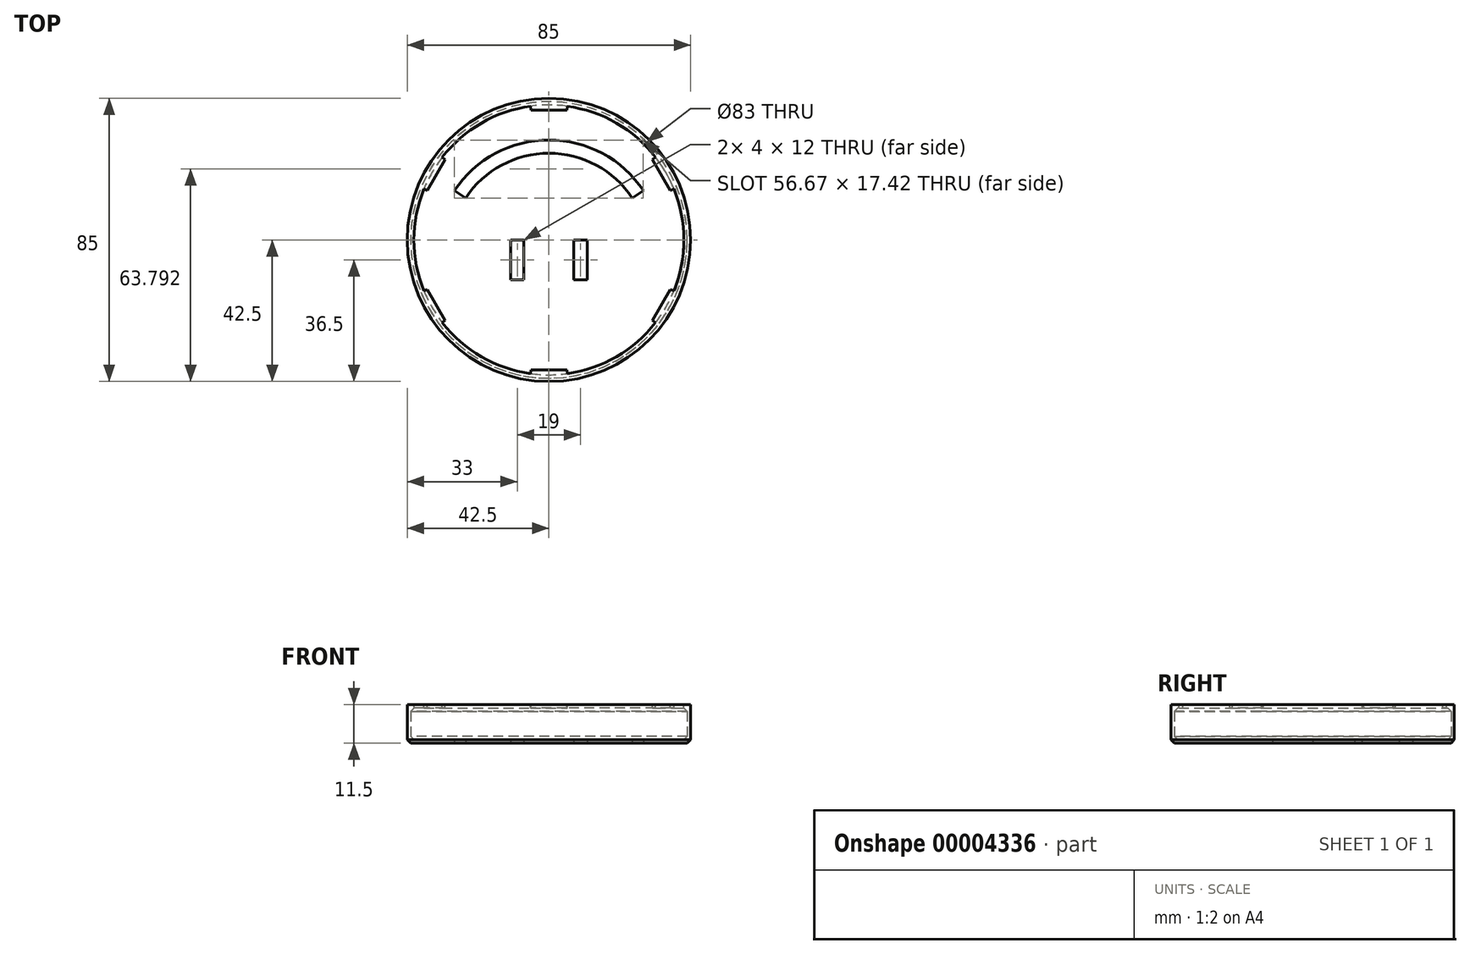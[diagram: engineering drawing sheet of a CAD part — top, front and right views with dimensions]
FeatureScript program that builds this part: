
annotation { "Feature Type Name" : "Feature", "Feature Type Description" : "" }
export const myFeature = defineFeature(function(context is Context, id is Id, definition is map)
    precondition{}
    {
        {
            var Q0;
            Q0=qCreatedBy(makeId("Top.planeOp"),FACE);
            var sketch = newSketch(context, id + "F0", { "sketchPlane" : qUnion([Q0])});
            skCircle(sketch, "E0", {"center": v(0, 0) * mm, "radius": 42.5 * mm});
            skSolve(sketch);
        }
        {
            var Q0;
            Q0 = qSketchRegion(id + "F0", true);
            extrude(context, id + "F1", {"entities" : qUnion([Q0]), "depth" : 11.5 * mm});
        }
        {
            var Q0;
            Q0=makeQuery(id+"F1.opExtrude","CAP_FACE",FACE,{"disambiguationData":[OSD([sQuery(id+"F0.wireOp",EDGE,"E0")])],"isStart":false});
            shell(context, id + "F2", {"entities" : qUnion([Q0]), "thickness" : 1 * mm});
        }
        {
            var Q0;
            Q0=makeQuery(id+"F1.opExtrude","CAP_FACE",FACE,{"disambiguationData":[OSD([sQuery(id+"F0.wireOp",EDGE,"E0")])],"isStart":false});
            var sketch = newSketch(context, id + "F3", { "sketchPlane" : qUnion([Q0])});
            skCircle(sketch, "E1", {"center": v(0, 0) * mm, "radius": 42.5 * mm});
            skCircle(sketch, "E2", {"center": v(0, 0) * mm, "radius": 40.5 * mm});
            skSolve(sketch);
        }
        {
            var Q0;
            Q0 = qSketchRegion(id + "F3", true);
            extrude(context, id + "F4", {"entities" : qUnion([Q0]), "operationType" : NewBodyOperationType.ADD, "oppositeDirection" : true, "depth" : 1 * mm});
        }
        {
            var Q0;
            Q0=makeQuery(id+"F4.boolean.opBoolean","MERGE",FACE,{"derivedFrom":[makeQuery(id+"F1.opExtrude","CAP_FACE",FACE,{"disambiguationData":[OSD([sQuery(id+"F0.wireOp",EDGE,"E0")])],"isStart":false}),makeQuery(id+"F4.opExtrude","CAP_FACE",FACE,{"disambiguationData":[OSD([sQuery(id+"F3.wireOp",EDGE,"E1"),sQuery(id+"F3.wireOp",EDGE,"E2")])],"isStart":true})]});
            var sketch = newSketch(context, id + "F5", { "sketchPlane" : qUnion([Q0])});
            skLineSegment(sketch, "E3", {"start": v(-5.5, 40.12) * mm, "end": v(-5.35, 39) * mm});
            skLineSegment(sketch, "E4", {"start": v(5.35, 39) * mm, "end": v(5.5, 40.12) * mm});
            skLineSegment(sketch, "E5", {"start": v(-5.5, 40.12) * mm, "end": v(-5.5, 40.5) * mm});
            skLineSegment(sketch, "E6", {"start": v(-5.5, 40.5) * mm, "end": v(5.5, 40.5) * mm});
            skLineSegment(sketch, "E7", {"start": v(5.5, 40.5) * mm, "end": v(5.5, 40.12) * mm});
            skLineSegment(sketch, "E8", {"start": v(-5.35, 39) * mm, "end": v(0, 39) * mm});
            skLineSegment(sketch, "E9", {"start": v(0, 39) * mm, "end": v(5.35, 39) * mm});
            skLineSegment(sketch, "E10", {"start": v(-5.5, 40.12) * mm, "end": v(-13.28, 39.06) * mm, "construction": true});
            skLineSegment(sketch, "E11", {"start": v(5.5, 40.12) * mm, "end": v(13.86, 38.98) * mm, "construction": true});
            skSolve(sketch);
        }
        {
            var Q0;
            Q0 = qSketchRegion(id + "F5", true);
            extrude(context, id + "F6", {"entities" : qUnion([Q0]), "operationType" : NewBodyOperationType.ADD, "oppositeDirection" : true, "depth" : 1 * mm});
        }
        {
            var Q0;
            Q0=qCreatedBy(makeId("Right.planeOp"),FACE);
            var sketch = newSketch(context, id + "F7", { "sketchPlane" : qUnion([Q0])});
            skLineSegment(sketch, "E12", {"start": v(0, 0) * mm, "end": v(0, 49.63) * mm, "construction": true});
            skSolve(sketch);
        }
        {
            var Q0;
            Q0=makeQuery(id+"F6.opExtrude","SWEPT_FACE",FACE,{"disambiguationData":[OSD([sQuery(id+"F5.wireOp",EDGE,"E4")])]});
            var Q1;
            Q1=makeQuery(id+"F6.opExtrude","SWEPT_FACE",FACE,{"disambiguationData":[OSD([sQuery(id+"F5.wireOp",EDGE,"E8"),sQuery(id+"F5.wireOp",EDGE,"E9")])]});
            var Q2;
            Q2=makeQuery(id+"F6.opExtrude","SWEPT_FACE",FACE,{"disambiguationData":[OSD([sQuery(id+"F5.wireOp",EDGE,"E3")])]});
            var Q3;
            Q3=sQuery(id+"F7.wireOp",EDGE,"E12");
            circularPattern(context, id + "F8", {"faces" : qUnion([Q0, Q1, Q2]), "axis" : qUnion([Q3]), "angle" : 60 * degree, "instanceCount" : 6, "patternType" : PatternType.FACE});
        }
        {
            var Q0;
            {var subQ0=sQuery(id+"F0.wireOp",EDGE,"E0");Q0=makeQuery(id+"F2.opShell","OFFSET_EDGE",EDGE,{"disambiguationData":[OSD([subQ0]),TDD([makeQuery(id+"F1.opExtrude","CAP_EDGE",EDGE,{"disambiguationData":[OSD([subQ0])],"isStart":true})])]});}
            chamfer(context, id + "F9", {"entities" : qUnion([Q0]), "width" : 1 * mm, "tangentPropagation" : true});
        }
        {
            var Q0;
            Q0=makeQuery(id+"F1.opExtrude","CAP_EDGE",EDGE,{"disambiguationData":[OSD([sQuery(id+"F0.wireOp",EDGE,"E0")])],"isStart":true});
            chamfer(context, id + "F10", {"entities" : qUnion([Q0]), "width" : 1 * mm, "tangentPropagation" : true});
        }
        {
            var Q0;
            Q0=makeQuery(id+"F1.opExtrude","CAP_FACE",FACE,{"disambiguationData":[OSD([sQuery(id+"F0.wireOp",EDGE,"E0")])],"isStart":true});
            var sketch = newSketch(context, id + "F11", { "sketchPlane" : qUnion([Q0])});
            skArc(sketch, "E13", {"start": v(-25, -12.58) * mm, "mid": v(0, -26) * mm, "end": v(25, -12.58) * mm});
            skArc(sketch, "E14", {"start": v(-28.33, -14.8) * mm, "mid": v(0, -30) * mm, "end": v(28.33, -14.8) * mm});
            skLineSegment(sketch, "E15", {"start": v(-28.33, -14.8) * mm, "end": v(-25, -12.58) * mm});
            skLineSegment(sketch, "E16", {"start": v(25, -12.58) * mm, "end": v(28.33, -14.8) * mm});
            skLineSegment(sketch, "E17", {"start": v(-28.33, -14.8) * mm, "end": v(0, -57.5) * mm, "construction": true});
            skLineSegment(sketch, "E18", {"start": v(0, -57.5) * mm, "end": v(28.33, -14.8) * mm, "construction": true});
            skLineSegment(sketch, "E19.bottom", {"start": v(-11.5, 12) * mm, "end": v(-7.5, 12) * mm});
            skLineSegment(sketch, "E19.top", {"start": v(-11.5, 0) * mm, "end": v(-7.5, 0) * mm});
            skLineSegment(sketch, "E19.left", {"start": v(-11.5, 12) * mm, "end": v(-11.5, 0) * mm});
            skLineSegment(sketch, "E19.right", {"start": v(-7.5, 12) * mm, "end": v(-7.5, 0) * mm});
            skLineSegment(sketch, "E20.bottom", {"start": v(7.5, 12) * mm, "end": v(11.5, 12) * mm});
            skLineSegment(sketch, "E20.top", {"start": v(7.5, 0) * mm, "end": v(11.5, 0) * mm});
            skLineSegment(sketch, "E20.left", {"start": v(7.5, 12) * mm, "end": v(7.5, 0) * mm});
            skLineSegment(sketch, "E20.right", {"start": v(11.5, 12) * mm, "end": v(11.5, 0) * mm});
            skLineSegment(sketch, "E21", {"start": v(0, 0) * mm, "end": v(0, 0) * mm});
            skLineSegment(sketch, "E22", {"start": v(0, 0) * mm, "end": v(7.5, 0) * mm, "construction": true});
            skLineSegment(sketch, "E23", {"start": v(0, 0) * mm, "end": v(-7.5, 0) * mm, "construction": true});
            skSolve(sketch);
        }
        {
            var Q0;
            Q0 = qSketchRegion(id + "F11", true);
            extrude(context, id + "F12", {"entities" : qUnion([Q0]), "operationType" : NewBodyOperationType.REMOVE, "oppositeDirection" : true, "depth" : 2 * mm});
        }
        {
            var Q0;
            {var subQ0=sQuery(id+"F0.wireOp",EDGE,"E0");Q0=makeQuery(id+"F4.boolean.opBoolean","INTERSECT",EDGE,{"derivedFrom":[makeQuery(id+"F2.opShell","OFFSET_FACE",FACE,{"disambiguationData":[OSD([subQ0]),TDD([makeQuery(id+"F1.opExtrude","SWEPT_FACE",FACE,{"disambiguationData":[OSD([subQ0])]})])]}),makeQuery(id+"F4.opExtrude","CAP_FACE",FACE,{"disambiguationData":[OSD([sQuery(id+"F3.wireOp",EDGE,"E1"),sQuery(id+"F3.wireOp",EDGE,"E2")])],"isStart":false})]});}
            chamfer(context, id + "F13", {"entities" : qUnion([Q0]), "width" : 1 * mm, "tangentPropagation" : true});
        }
    });
